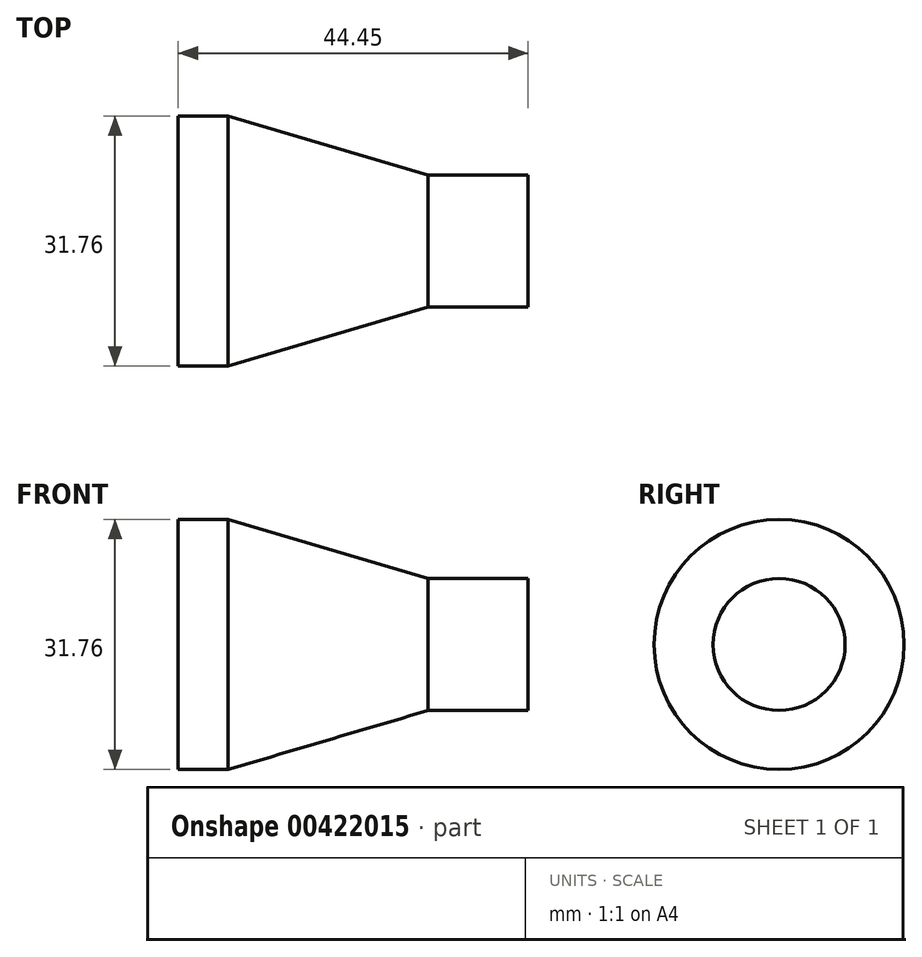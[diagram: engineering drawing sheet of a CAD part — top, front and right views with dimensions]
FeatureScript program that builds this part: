
annotation { "Feature Type Name" : "Feature", "Feature Type Description" : "" }
export const myFeature = defineFeature(function(context is Context, id is Id, definition is map)
    precondition{}
    {
        {
            var Q0;
            Q0=qCreatedBy(makeId("Right.planeOp"),FACE);
            var sketch = newSketch(context, id + "F0", { "sketchPlane" : qUnion([Q0])});
            skCircle(sketch, "E0", {"center": v(0, 0) * mm, "radius": 15.88 * mm});
            skSolve(sketch);
        }
        {
            var Q0;
            Q0 = qSketchRegion(id + "F0", true);
            extrude(context, id + "F1", {"entities" : qUnion([Q0]), "depth" : 6.35 * mm});
        }
        {
            var Q0;
            Q0=makeQuery(id+"F1.opExtrude","CAP_FACE",FACE,{"disambiguationData":[OSD([sQuery(id+"F0.wireOp",EDGE,"E0")])],"isStart":false});
            cPlane(context, id + "F2", {"entities" : qUnion([Q0]), "cplaneType" : CPlaneType.OFFSET, "offset" : 25.4 * mm, "width" : 152.4 * mm, "height" : 152.4 * mm});
        }
        {
            var Q0;
            Q0=qCreatedBy(id+"F2.planeOp",FACE);
            var sketch = newSketch(context, id + "F3", { "sketchPlane" : qUnion([Q0])});
            skCircle(sketch, "E1", {"center": v(0, 0) * mm, "radius": 8.38 * mm});
            skSolve(sketch);
        }
        {
            var Q1;
            Q1=makeQuery(id+"F1.opExtrude","CAP_FACE",FACE,{"disambiguationData":[OSD([sQuery(id+"F0.wireOp",EDGE,"E0")])],"isStart":false});
            var Q2;
            Q2=makeQuery(id+"F3.imprint","IMPRINT",FACE,{"disambiguationData":[TD([[makeQuery(id+"F3.imprint","IMPRINT",EDGE,{"derivedFrom":sQuery(id+"F3.wireOp",EDGE,"E1")}),1.0]])]});
            loft(context, id + "F4", {"operationType" : NewBodyOperationType.ADD, "sheetProfilesArray" : [{ "sheetProfileEntities" : qUnion([Q1]) }, { "sheetProfileEntities" : qUnion([Q2]) }]});
        }
        {
            var Q0;
            Q0=makeQuery(id+"F4.opLoft","CAP_FACE",FACE,{"disambiguationData":[OSD([makeQuery(id+"F3.imprint","IMPRINT",FACE,{"disambiguationData":[TD([[makeQuery(id+"F3.imprint","IMPRINT",EDGE,{"derivedFrom":sQuery(id+"F3.wireOp",EDGE,"E1")}),1.0]])]})])],"isStart":true});
            var sketch = newSketch(context, id + "F5", { "sketchPlane" : qUnion([Q0])});
            skCircle(sketch, "E2.0", {"center": v(0, 0) * mm, "radius": 8.38 * mm});
            skSolve(sketch);
        }
        {
            var Q0;
            Q0 = qSketchRegion(id + "F5", true);
            extrude(context, id + "F6", {"entities" : qUnion([Q0]), "operationType" : NewBodyOperationType.ADD, "depth" : 12.7 * mm});
        }
    });
